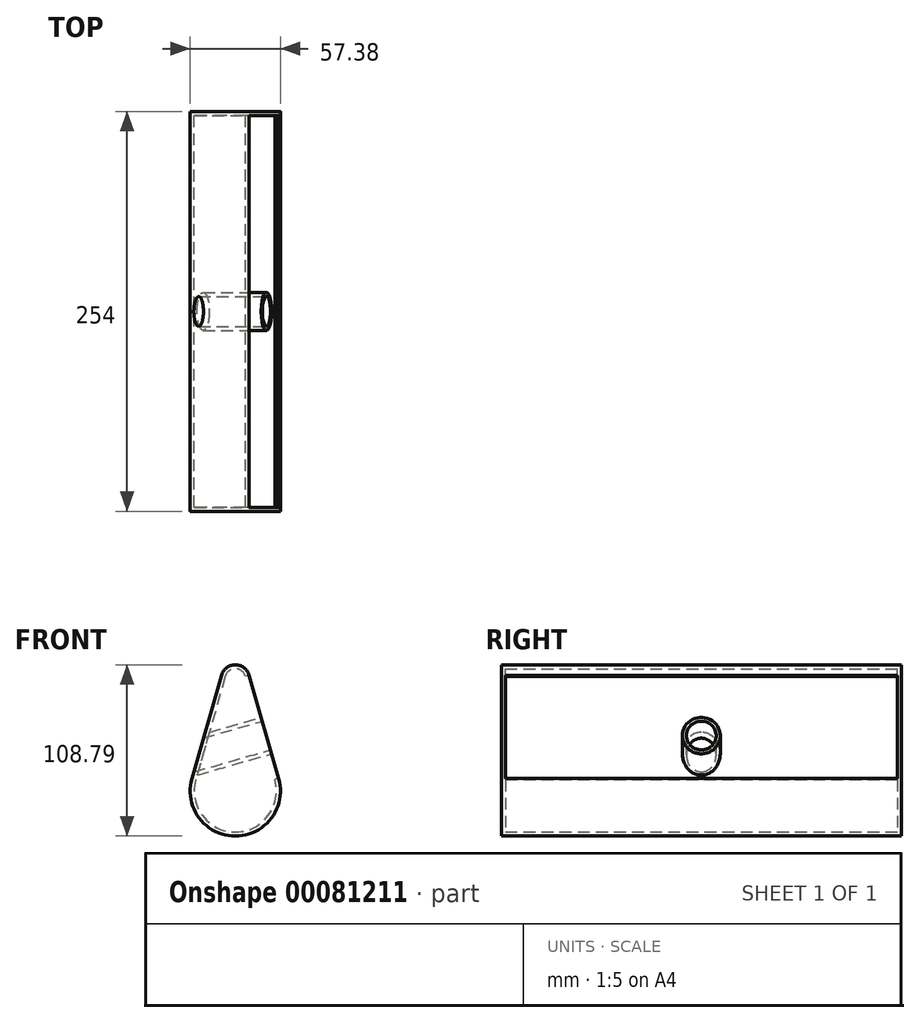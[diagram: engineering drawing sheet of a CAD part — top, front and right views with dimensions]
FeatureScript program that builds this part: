
annotation { "Feature Type Name" : "Feature", "Feature Type Description" : "" }
export const myFeature = defineFeature(function(context is Context, id is Id, definition is map)
    precondition{}
    {
        {
            var Q0;
            Q0=qCreatedBy(makeId("Front.planeOp"),FACE);
            var sketch = newSketch(context, id + "F0", { "sketchPlane" : qUnion([Q0])});
            skArc(sketch, "E0", {"start": v(-27.58, -0.53) * mm, "mid": v(0, -37.11) * mm, "end": v(27.58, -0.53) * mm});
            skArc(sketch, "E1", {"start": v(8.8, 65.04) * mm, "mid": v(0, 71.68) * mm, "end": v(-8.8, 65.04) * mm});
            skLineSegment(sketch, "E2", {"start": v(8.8, 65.04) * mm, "end": v(27.58, -0.53) * mm});
            skLineSegment(sketch, "E3", {"start": v(-8.8, 65.04) * mm, "end": v(-27.58, -0.53) * mm});
            skSolve(sketch);
        }
        {
            var Q0;
            Q0=makeQuery(id+"F0.imprint","IMPRINT",FACE,{"disambiguationData":[TD([[makeQuery(id+"F0.imprint","IMPRINT",EDGE,{"derivedFrom":sQuery(id+"F0.wireOp",EDGE,"E0")}),1.0]])]});
            extrude(context, id + "F1", {"entities" : qUnion([Q0]), "depth" : 254 * mm});
        }
        {
            var Q0;
            Q0=makeQuery(id+"F1.opExtrude","SWEPT_FACE",FACE,{"disambiguationData":[OSD([sQuery(id+"F0.wireOp",EDGE,"E2")])]});
            var sketch = newSketch(context, id + "F2", { "sketchPlane" : qUnion([Q0])});
            skCircle(sketch, "E4", {"center": v(-127, 20.27) * mm, "radius": 9.47 * mm});
            skSolve(sketch);
        }
        {
            var Q0;
            Q0=makeQuery(id+"F2.imprint","IMPRINT",FACE,{"disambiguationData":[TD([[makeQuery(id+"F2.imprint","IMPRINT",EDGE,{"derivedFrom":sQuery(id+"F2.wireOp",EDGE,"E4")}),1.0]])]});
            extrude(context, id + "F3", {"entities" : qUnion([Q0]), "operationType" : NewBodyOperationType.REMOVE, "endBound" : BoundingType.THROUGH_ALL, "oppositeDirection" : true, "depth" : 25.4 * mm});
        }
        {
            var Q0;
            Q0=makeQuery(id+"F1.opExtrude","SWEPT_FACE",FACE,{"disambiguationData":[OSD([sQuery(id+"F0.wireOp",EDGE,"E2")])]});
            shell(context, id + "F4", {"entities" : qUnion([Q0]), "thickness" : 2.54 * mm});
        }
    });
